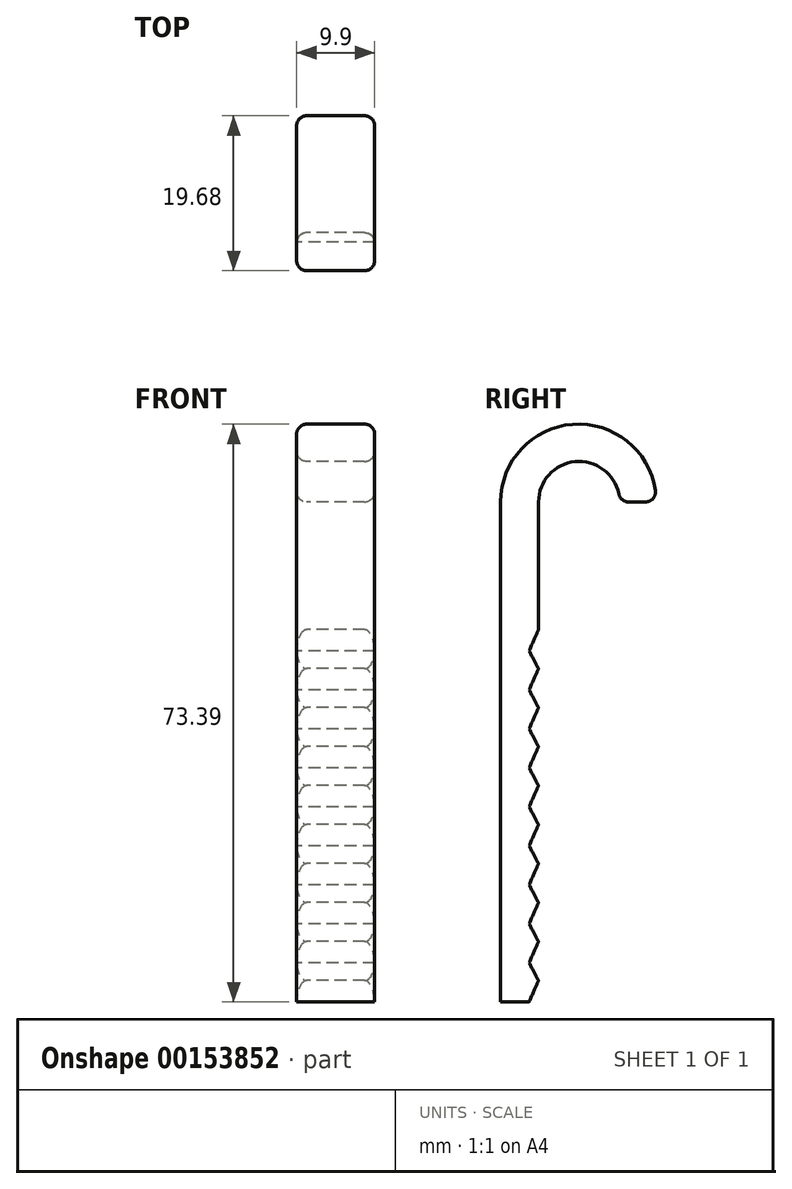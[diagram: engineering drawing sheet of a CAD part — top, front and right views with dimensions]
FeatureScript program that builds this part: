
annotation { "Feature Type Name" : "Feature", "Feature Type Description" : "" }
export const myFeature = defineFeature(function(context is Context, id is Id, definition is map)
    precondition{}
    {
        {
            var Q0;
            Q0=qCreatedBy(makeId("Top.planeOp"),FACE);
            var sketch = newSketch(context, id + "F0", { "sketchPlane" : qUnion([Q0])});
            skLineSegment(sketch, "E0.bottom", {"start": v(4.95, -2.41) * mm, "end": v(-4.95, -2.41) * mm});
            skLineSegment(sketch, "E0.top", {"start": v(4.95, 2.41) * mm, "end": v(-4.95, 2.41) * mm});
            skLineSegment(sketch, "E0.left", {"start": v(4.95, -2.41) * mm, "end": v(4.95, 2.41) * mm});
            skLineSegment(sketch, "E0.right", {"start": v(-4.95, -2.41) * mm, "end": v(-4.95, 2.41) * mm});
            skPoint(sketch, "E0.middle", {"position": v(0, 0) * mm});
            skSolve(sketch);
        }
        {
            var Q0;
            Q0 = qSketchRegion(id + "F0", true);
            extrude(context, id + "F1", {"entities" : qUnion([Q0]), "depth" : 63.5 * mm});
        }
        {
            var Q0;
            Q0=makeQuery(id+"F1.opExtrude","SWEPT_FACE",FACE,{"disambiguationData":[OSD([sQuery(id+"F0.wireOp",EDGE,"E0.right")])]});
            var sketch = newSketch(context, id + "F2", { "sketchPlane" : qUnion([Q0])});
            skLineSegment(sketch, "E1", {"start": v(-1.21, 0) * mm, "end": v(-2.41, 2.7) * mm});
            skLineSegment(sketch, "E2", {"start": v(-2.41, 2.7) * mm, "end": v(-1.21, 4.97) * mm});
            skLineSegment(sketch, "E3", {"start": v(-1.21, 4.97) * mm, "end": v(-1.21, 0) * mm});
            skLineSegment(sketch, "E4.0.1.0", {"start": v(-2.41, 7.65) * mm, "end": v(-1.21, 9.92) * mm});
            skLineSegment(sketch, "E4.0.1.1", {"start": v(-1.21, 4.95) * mm, "end": v(-2.41, 7.65) * mm});
            skLineSegment(sketch, "E4.0.1.2", {"start": v(-1.21, 9.92) * mm, "end": v(-1.21, 4.95) * mm});
            skLineSegment(sketch, "E4.0.2.0", {"start": v(-2.41, 12.6) * mm, "end": v(-1.21, 14.88) * mm});
            skLineSegment(sketch, "E4.0.2.1", {"start": v(-1.21, 9.9) * mm, "end": v(-2.41, 12.6) * mm});
            skLineSegment(sketch, "E4.0.2.2", {"start": v(-1.21, 14.88) * mm, "end": v(-1.21, 9.9) * mm});
            skLineSegment(sketch, "E4.0.3.0", {"start": v(-2.41, 17.55) * mm, "end": v(-1.21, 19.83) * mm});
            skLineSegment(sketch, "E4.0.3.1", {"start": v(-1.21, 14.86) * mm, "end": v(-2.41, 17.55) * mm});
            skLineSegment(sketch, "E4.0.3.2", {"start": v(-1.21, 19.83) * mm, "end": v(-1.21, 14.86) * mm});
            skLineSegment(sketch, "E4.0.4.0", {"start": v(-2.41, 22.5) * mm, "end": v(-1.21, 24.78) * mm});
            skLineSegment(sketch, "E4.0.4.1", {"start": v(-1.21, 19.81) * mm, "end": v(-2.41, 22.5) * mm});
            skLineSegment(sketch, "E4.0.4.2", {"start": v(-1.21, 24.78) * mm, "end": v(-1.21, 19.81) * mm});
            skLineSegment(sketch, "E4.0.5.0", {"start": v(-2.41, 27.46) * mm, "end": v(-1.21, 29.74) * mm});
            skLineSegment(sketch, "E4.0.5.1", {"start": v(-1.21, 24.77) * mm, "end": v(-2.41, 27.46) * mm});
            skLineSegment(sketch, "E4.0.5.2", {"start": v(-1.21, 29.74) * mm, "end": v(-1.21, 24.77) * mm});
            skLineSegment(sketch, "E4.0.6.0", {"start": v(-2.41, 32.41) * mm, "end": v(-1.21, 34.69) * mm});
            skLineSegment(sketch, "E4.0.6.1", {"start": v(-1.21, 29.72) * mm, "end": v(-2.41, 32.41) * mm});
            skLineSegment(sketch, "E4.0.6.2", {"start": v(-1.21, 34.69) * mm, "end": v(-1.21, 29.72) * mm});
            skLineSegment(sketch, "E4.0.7.0", {"start": v(-2.41, 37.36) * mm, "end": v(-1.21, 39.64) * mm});
            skLineSegment(sketch, "E4.0.7.1", {"start": v(-1.21, 34.67) * mm, "end": v(-2.41, 37.36) * mm});
            skLineSegment(sketch, "E4.0.7.2", {"start": v(-1.21, 39.64) * mm, "end": v(-1.21, 34.67) * mm});
            skLineSegment(sketch, "E4.0.8.0", {"start": v(-2.41, 42.32) * mm, "end": v(-1.21, 44.6) * mm});
            skLineSegment(sketch, "E4.0.8.1", {"start": v(-1.21, 39.62) * mm, "end": v(-2.41, 42.32) * mm});
            skLineSegment(sketch, "E4.0.8.2", {"start": v(-1.21, 44.6) * mm, "end": v(-1.21, 39.62) * mm});
            skLineSegment(sketch, "E4.0.9.0", {"start": v(-2.41, 47.27) * mm, "end": v(-1.21, 49.55) * mm});
            skLineSegment(sketch, "E4.0.9.1", {"start": v(-1.21, 44.58) * mm, "end": v(-2.41, 47.27) * mm});
            skLineSegment(sketch, "E4.0.9.2", {"start": v(-1.21, 49.55) * mm, "end": v(-1.21, 44.58) * mm});
            skLineSegment(sketch, "E4.direction1", {"start": v(-2.41, 2.7) * mm, "end": v(22.99, 2.7) * mm, "construction": true});
            skLineSegment(sketch, "E4.direction2", {"start": v(-2.41, 2.7) * mm, "end": v(-2.41, 7.65) * mm, "construction": true});
            skSolve(sketch);
        }
        {
            var Q0;
            {var subQ0=sQuery(id+"F2.wireOp",EDGE,"E1");Q0=makeQuery(id+"F2.imprint","IMPRINT",FACE,{"disambiguationData":[TD([[makeQuery(id+"F2.imprint","IMPRINT",EDGE,{"derivedFrom":subQ0}),1.0]])]});}
            var Q1;
            {var subQ0=sQuery(id+"F2.wireOp",EDGE,"E2");var subQ3=sQuery(id+"F2.wireOp",EDGE,"E4.0.1.1");var subQ4=makeQuery(id+"F2.imprint","INTERSECT",VERTEX,{"derivedFrom":[subQ0,subQ3]});Q1=makeQuery(id+"F2.imprint","IMPRINT",FACE,{"disambiguationData":[TD([[makeQuery(id+"F2.imprint","IMPRINT",EDGE,{"disambiguationData":[TD([[subQ4,1.0]])],"derivedFrom":subQ0}),1.0]])]});}
            var Q2;
            {var subQ0=sQuery(id+"F2.wireOp",EDGE,"E4.0.1.0");var subQ3=sQuery(id+"F2.wireOp",EDGE,"E4.0.2.1");var subQ4=makeQuery(id+"F2.imprint","INTERSECT",VERTEX,{"derivedFrom":[subQ0,subQ3]});Q2=makeQuery(id+"F2.imprint","IMPRINT",FACE,{"disambiguationData":[TD([[makeQuery(id+"F2.imprint","IMPRINT",EDGE,{"disambiguationData":[TD([[subQ4,1.0]])],"derivedFrom":subQ0}),1.0]])]});}
            var Q3;
            {var subQ0=sQuery(id+"F2.wireOp",EDGE,"E4.0.2.0");var subQ3=sQuery(id+"F2.wireOp",EDGE,"E4.0.3.1");var subQ4=makeQuery(id+"F2.imprint","INTERSECT",VERTEX,{"derivedFrom":[subQ0,subQ3]});Q3=makeQuery(id+"F2.imprint","IMPRINT",FACE,{"disambiguationData":[TD([[makeQuery(id+"F2.imprint","IMPRINT",EDGE,{"disambiguationData":[TD([[subQ4,1.0]])],"derivedFrom":subQ0}),1.0]])]});}
            var Q4;
            {var subQ0=sQuery(id+"F2.wireOp",EDGE,"E4.0.3.0");var subQ3=sQuery(id+"F2.wireOp",EDGE,"E4.0.4.1");var subQ4=makeQuery(id+"F2.imprint","INTERSECT",VERTEX,{"derivedFrom":[subQ0,subQ3]});Q4=makeQuery(id+"F2.imprint","IMPRINT",FACE,{"disambiguationData":[TD([[makeQuery(id+"F2.imprint","IMPRINT",EDGE,{"disambiguationData":[TD([[subQ4,1.0]])],"derivedFrom":subQ0}),1.0]])]});}
            var Q5;
            {var subQ0=sQuery(id+"F2.wireOp",EDGE,"E4.0.4.0");var subQ3=sQuery(id+"F2.wireOp",EDGE,"E4.0.5.1");var subQ4=makeQuery(id+"F2.imprint","INTERSECT",VERTEX,{"derivedFrom":[subQ0,subQ3]});Q5=makeQuery(id+"F2.imprint","IMPRINT",FACE,{"disambiguationData":[TD([[makeQuery(id+"F2.imprint","IMPRINT",EDGE,{"disambiguationData":[TD([[subQ4,1.0]])],"derivedFrom":subQ0}),1.0]])]});}
            var Q6;
            {var subQ0=sQuery(id+"F2.wireOp",EDGE,"E4.0.5.0");var subQ3=sQuery(id+"F2.wireOp",EDGE,"E4.0.6.1");var subQ4=makeQuery(id+"F2.imprint","INTERSECT",VERTEX,{"derivedFrom":[subQ0,subQ3]});Q6=makeQuery(id+"F2.imprint","IMPRINT",FACE,{"disambiguationData":[TD([[makeQuery(id+"F2.imprint","IMPRINT",EDGE,{"disambiguationData":[TD([[subQ4,1.0]])],"derivedFrom":subQ0}),1.0]])]});}
            var Q7;
            {var subQ0=sQuery(id+"F2.wireOp",EDGE,"E4.0.6.0");var subQ3=sQuery(id+"F2.wireOp",EDGE,"E4.0.7.1");var subQ4=makeQuery(id+"F2.imprint","INTERSECT",VERTEX,{"derivedFrom":[subQ0,subQ3]});Q7=makeQuery(id+"F2.imprint","IMPRINT",FACE,{"disambiguationData":[TD([[makeQuery(id+"F2.imprint","IMPRINT",EDGE,{"disambiguationData":[TD([[subQ4,1.0]])],"derivedFrom":subQ0}),1.0]])]});}
            var Q8;
            {var subQ0=sQuery(id+"F2.wireOp",EDGE,"E4.0.7.0");var subQ3=sQuery(id+"F2.wireOp",EDGE,"E4.0.8.1");var subQ4=makeQuery(id+"F2.imprint","INTERSECT",VERTEX,{"derivedFrom":[subQ0,subQ3]});Q8=makeQuery(id+"F2.imprint","IMPRINT",FACE,{"disambiguationData":[TD([[makeQuery(id+"F2.imprint","IMPRINT",EDGE,{"disambiguationData":[TD([[subQ4,1.0]])],"derivedFrom":subQ0}),1.0]])]});}
            var Q9;
            {var subQ0=sQuery(id+"F2.wireOp",EDGE,"E4.0.8.0");var subQ3=sQuery(id+"F2.wireOp",EDGE,"E4.0.9.1");var subQ4=makeQuery(id+"F2.imprint","INTERSECT",VERTEX,{"derivedFrom":[subQ0,subQ3]});Q9=makeQuery(id+"F2.imprint","IMPRINT",FACE,{"disambiguationData":[TD([[makeQuery(id+"F2.imprint","IMPRINT",EDGE,{"disambiguationData":[TD([[subQ4,1.0]])],"derivedFrom":subQ0}),1.0]])]});}
            extrude(context, id + "F3", {"entities" : qUnion([Q0, Q1, Q2, Q3, Q4, Q5, Q6, Q7, Q8, Q9]), "operationType" : NewBodyOperationType.REMOVE, "endBound" : BoundingType.UP_TO_NEXT, "oppositeDirection" : true, "depth" : 25.4 * mm});
        }
        {
            var Q0;
            Q0=makeQuery(id+"F1.opExtrude","SWEPT_FACE",FACE,{"disambiguationData":[OSD([sQuery(id+"F0.wireOp",EDGE,"E0.right")])]});
            var sketch = newSketch(context, id + "F4", { "sketchPlane" : qUnion([Q0])});
            skArc(sketch, "E5", {"start": v(-2.41, 63.5) * mm, "mid": v(-7.56, 68.65) * mm, "end": v(-12.7, 63.5) * mm});
            skArc(sketch, "E6", {"start": v(2.41, 63.5) * mm, "mid": v(-7.48, 73.39) * mm, "end": v(-17.37, 63.5) * mm});
            skLineSegment(sketch, "E7", {"start": v(-17.37, 63.5) * mm, "end": v(-12.7, 63.5) * mm});
            skLineSegment(sketch, "E8", {"start": v(-2.41, 63.5) * mm, "end": v(2.41, 63.5) * mm});
            skSolve(sketch);
        }
        {
            var Q0;
            Q0 = qSketchRegion(id + "F4", true);
            extrude(context, id + "F5", {"entities" : qUnion([Q0]), "operationType" : NewBodyOperationType.ADD, "oppositeDirection" : true, "depth" : 9.9 * mm});
        }
        {
            var Q0;
            Q0=makeQuery(id+"F5.opExtrude","SWEPT_FACE",FACE,{"disambiguationData":[OSD([sQuery(id+"F4.wireOp",EDGE,"E7")])]});
            var Q1;
            Q1=makeQuery(id+"F5.opExtrude","CAP_EDGE",EDGE,{"disambiguationData":[OSD([sQuery(id+"F4.wireOp",EDGE,"E6")])],"isStart":true});
            var Q2;
            Q2=makeQuery(id+"F5.opExtrude","CAP_EDGE",EDGE,{"disambiguationData":[OSD([sQuery(id+"F4.wireOp",EDGE,"E6")])],"isStart":false});
            var Q3;
            Q3=makeQuery(id+"F5.opExtrude","CAP_EDGE",EDGE,{"disambiguationData":[OSD([sQuery(id+"F4.wireOp",EDGE,"E5")])],"isStart":true});
            var Q4;
            Q4=makeQuery(id+"F5.opExtrude","CAP_EDGE",EDGE,{"disambiguationData":[OSD([sQuery(id+"F4.wireOp",EDGE,"E5")])],"isStart":false});
            fillet(context, id + "F6", {"entities" : qUnion([Q0, Q1, Q2, Q3, Q4]), "radius" : 1.27 * mm, "tangentPropagation" : true, "allowEdgeOverflow" : false});
        }
    });
